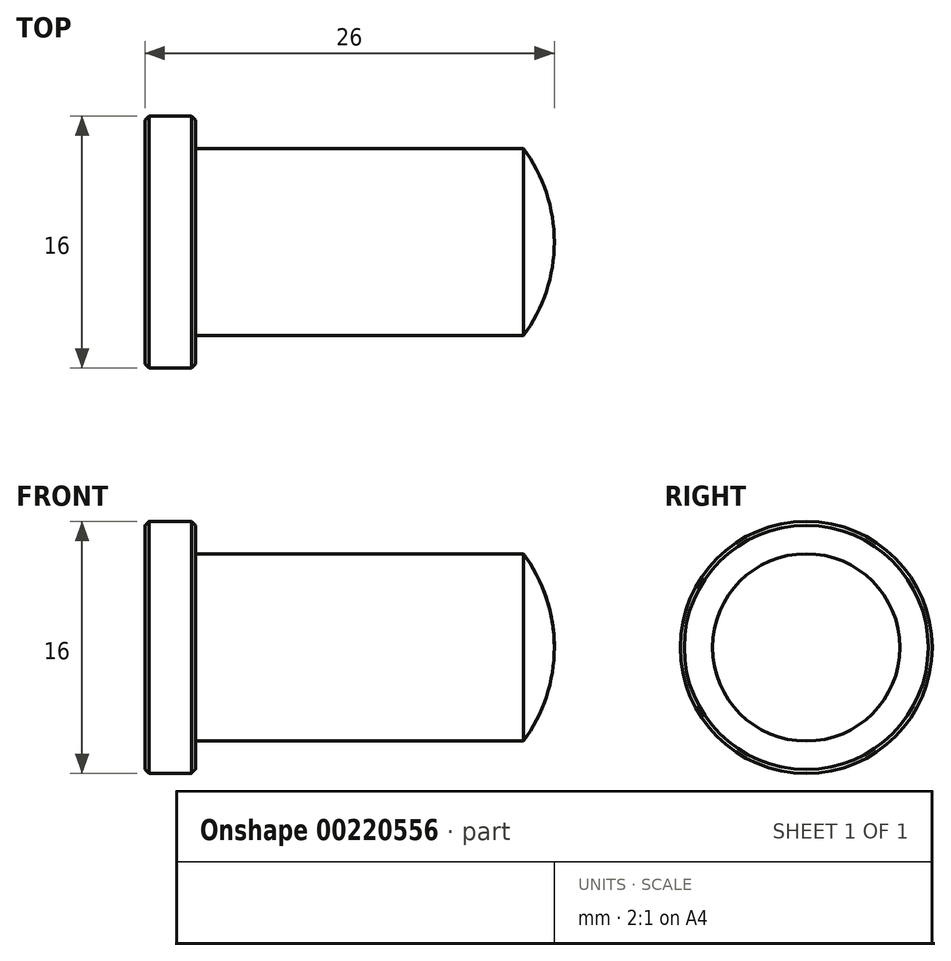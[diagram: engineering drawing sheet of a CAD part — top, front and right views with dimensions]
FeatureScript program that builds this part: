
annotation { "Feature Type Name" : "Feature", "Feature Type Description" : "" }
export const myFeature = defineFeature(function(context is Context, id is Id, definition is map)
    precondition{}
    {
        {
            var Q0;
            Q0=qCreatedBy(makeId("Front.planeOp"),FACE);
            var sketch = newSketch(context, id + "F0", { "sketchPlane" : qUnion([Q0]), "disableImprinting" : false});
            skLineSegment(sketch, "E0", {"start": v(0, 0) * mm, "end": v(0, 8) * mm});
            skLineSegment(sketch, "E1", {"start": v(0, 8) * mm, "end": v(3.2, 8) * mm});
            skLineSegment(sketch, "E2", {"start": v(3.2, 8) * mm, "end": v(3.2, 5.95) * mm});
            skLineSegment(sketch, "E3", {"start": v(3.2, 5.95) * mm, "end": v(24.04, 5.95) * mm});
            skLineSegment(sketch, "E4", {"start": v(0, 0) * mm, "end": v(16, 0) * mm, "construction": true});
            skArc(sketch, "E5", {"start": v(24.04, 5.95) * mm, "mid": v(25.5, 3.13) * mm, "end": v(26, 0) * mm});
            skLineSegment(sketch, "E6", {"start": v(0, 0) * mm, "end": v(26, 0) * mm});
            skSolve(sketch);
        }
        {
            var Q0;
            Q0=makeQuery(id+"F0.imprint","IMPRINT",FACE,{"disambiguationData":[TD([[makeQuery(id+"F0.imprint","IMPRINT",EDGE,{"derivedFrom":sQuery(id+"F0.wireOp",EDGE,"E0")}),-1.0]])]});
            var Q1;
            Q1=sQuery(id+"F0.wireOp",EDGE,"E1");
            var Q2;
            Q2=sQuery(id+"F0.wireOp",EDGE,"E0");
            var Q3;
            Q3=sQuery(id+"F0.wireOp",EDGE,"E2");
            var Q4;
            Q4=sQuery(id+"F0.wireOp",EDGE,"E3");
            var Q5;
            Q5=sQuery(id+"F0.wireOp",EDGE,"E5");
            var Q6;
            Q6=sQuery(id+"F0.wireOp",EDGE,"E4");
            revolve(context, id + "F1", {"entities" : qUnion([Q0]), "surfaceEntities" : qUnion([Q1, Q2, Q3, Q4, Q5]), "axis" : qUnion([Q6]), "revolveType" : RevolveType.FULL});
        }
        {
            var Q0;
            Q0=makeQuery(id+"F1.opRevolve","SWEPT_EDGE",EDGE,{"disambiguationData":[OSD([sQuery(id+"F0.wireOp",EDGE,"E1"),sQuery(id+"F0.wireOp",EDGE,"E2")])]});
            chamfer(context, id + "F2", {"entities" : qUnion([Q0]), "width" : .25 * mm, "tangentPropagation" : true});
        }
        {
            var Q0;
            Q0=makeQuery(id+"F1.opRevolve","SWEPT_EDGE",EDGE,{"disambiguationData":[OSD([sQuery(id+"F0.wireOp",EDGE,"E0"),sQuery(id+"F0.wireOp",EDGE,"E1")])]});
            chamfer(context, id + "F3", {"entities" : qUnion([Q0]), "width" : .25 * mm, "tangentPropagation" : true});
        }
        {
            var Q0;
            Q0=makeQuery(id+"F1.opRevolve","SWEPT_EDGE",EDGE,{"disambiguationData":[OSD([sQuery(id+"F0.wireOp",EDGE,"E2"),sQuery(id+"F0.wireOp",EDGE,"E3")])]});
            fillet(context, id + "F4", {"entities" : qUnion([Q0]), "radius" : .1 * mm, "tangentPropagation" : true, "allowEdgeOverflow" : false});
        }
    });
